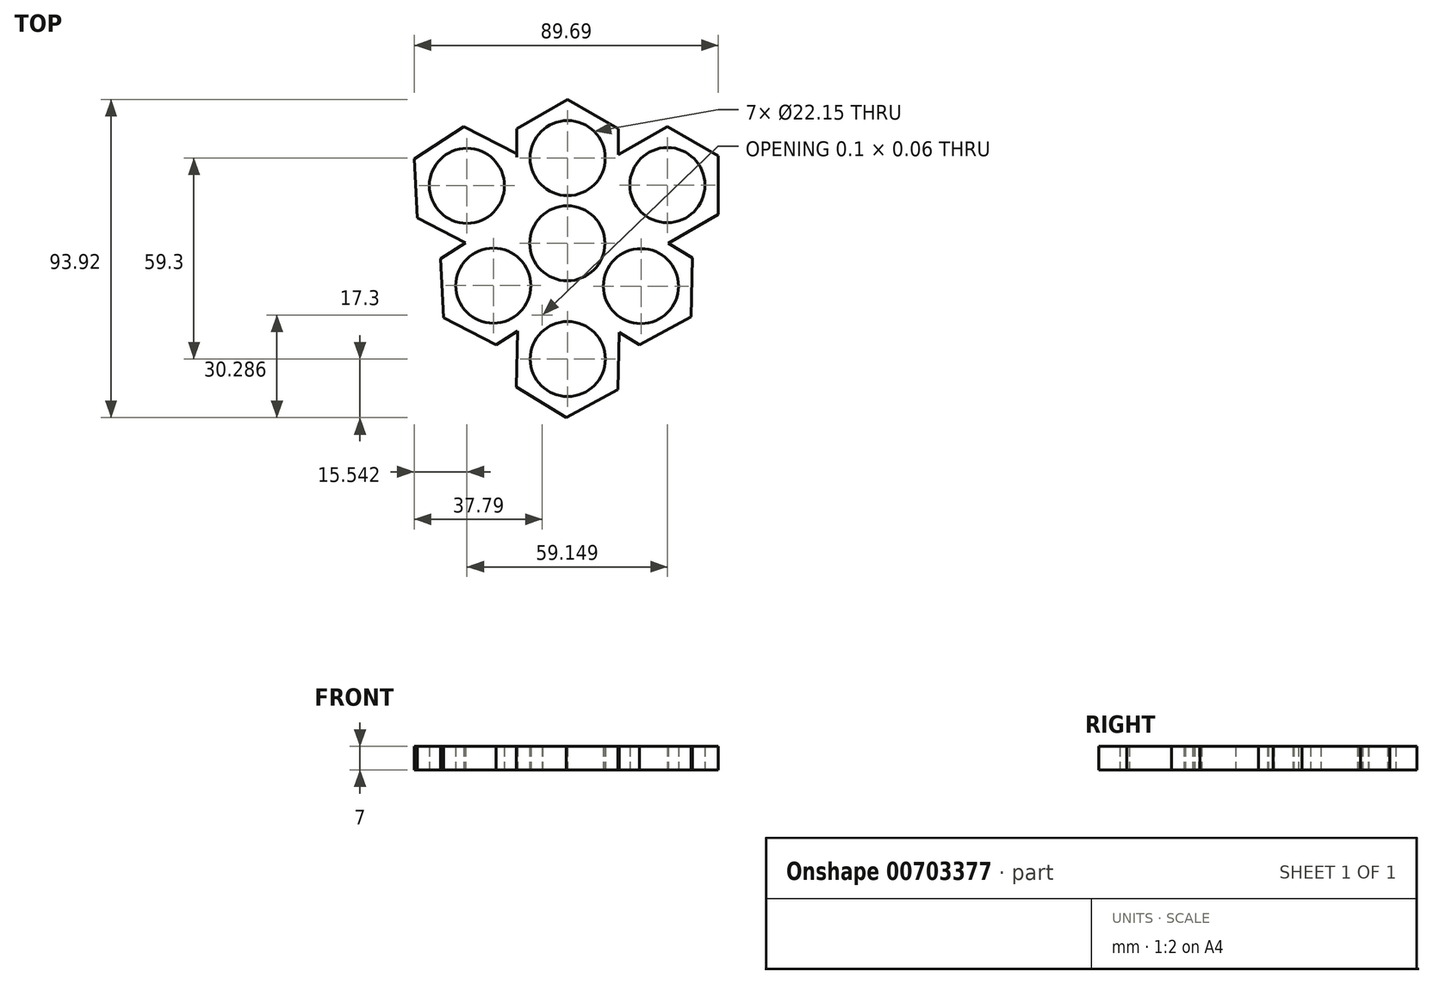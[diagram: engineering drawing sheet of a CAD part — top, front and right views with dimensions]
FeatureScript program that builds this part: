
annotation { "Feature Type Name" : "Feature", "Feature Type Description" : "" }
export const myFeature = defineFeature(function(context is Context, id is Id, definition is map)
    precondition{}
    {
        {
            var Q0;
            Q0=qCreatedBy(makeId("Top.planeOp"),FACE);
            var sketch = newSketch(context, id + "F0", { "sketchPlane" : qUnion([Q0])});
            skCircle(sketch, "E0.cCircle", {"center": v(0, 0) * mm, "radius": 12.57 * mm, "construction": true});
            skLineSegment(sketch, "E0.0", {"start": v(0.1, 25.15) * mm, "end": v(21.73, -12.66) * mm});
            skLineSegment(sketch, "E0.1", {"start": v(21.73, -12.66) * mm, "end": v(-21.83, -12.5) * mm});
            skLineSegment(sketch, "E0.2", {"start": v(-21.83, -12.5) * mm, "end": v(0.1, 25.15) * mm});
            skPoint(sketch, "E0.0.midPoint", {"position": v(10.91, 6.25) * mm});
            skCircle(sketch, "E1.cCircle", {"center": v(0.1, 25.15) * mm, "radius": 15 * mm, "construction": true});
            skLineSegment(sketch, "E1.0", {"start": v(15.1, 33.81) * mm, "end": v(15.1, 16.49) * mm});
            skLineSegment(sketch, "E1.1", {"start": v(15.1, 16.49) * mm, "end": v(0.1, 7.83) * mm});
            skLineSegment(sketch, "E1.2", {"start": v(0.1, 7.83) * mm, "end": v(-14.9, 16.49) * mm});
            skLineSegment(sketch, "E1.3", {"start": v(-14.9, 16.49) * mm, "end": v(-14.9, 33.81) * mm});
            skLineSegment(sketch, "E1.4", {"start": v(-14.9, 33.81) * mm, "end": v(0.1, 42.47) * mm});
            skLineSegment(sketch, "E1.5", {"start": v(0.1, 42.47) * mm, "end": v(15.1, 33.81) * mm});
            skPoint(sketch, "E1.0.midPoint", {"position": v(15.1, 25.15) * mm});
            skCircle(sketch, "E2.cCircle", {"center": v(21.73, -12.66) * mm, "radius": 14.99 * mm, "construction": true});
            skLineSegment(sketch, "E2.0", {"start": v(36.92, -4.34) * mm, "end": v(36.52, -21.65) * mm});
            skLineSegment(sketch, "E2.1", {"start": v(36.52, -21.65) * mm, "end": v(21.34, -29.96) * mm});
            skLineSegment(sketch, "E2.2", {"start": v(21.34, -29.96) * mm, "end": v(6.55, -20.97) * mm});
            skLineSegment(sketch, "E2.3", {"start": v(6.55, -20.97) * mm, "end": v(6.95, -3.66) * mm});
            skLineSegment(sketch, "E2.4", {"start": v(6.95, -3.66) * mm, "end": v(22.13, 4.65) * mm});
            skLineSegment(sketch, "E2.5", {"start": v(22.13, 4.65) * mm, "end": v(36.92, -4.34) * mm});
            skPoint(sketch, "E2.0.midPoint", {"position": v(36.72, -13) * mm});
            skCircle(sketch, "E3.cCircle", {"center": v(-21.83, -12.5) * mm, "radius": 15.12 * mm, "construction": true});
            skLineSegment(sketch, "E3.0", {"start": v(-20.96, -29.93) * mm, "end": v(-36.5, -21.97) * mm});
            skLineSegment(sketch, "E3.1", {"start": v(-36.5, -21.97) * mm, "end": v(-37.37, -4.53) * mm});
            skLineSegment(sketch, "E3.2", {"start": v(-37.37, -4.53) * mm, "end": v(-22.7, 4.95) * mm});
            skLineSegment(sketch, "E3.3", {"start": v(-22.7, 4.95) * mm, "end": v(-7.16, -3.02) * mm});
            skLineSegment(sketch, "E3.4", {"start": v(-7.16, -3.02) * mm, "end": v(-6.29, -20.46) * mm});
            skLineSegment(sketch, "E3.5", {"start": v(-6.29, -20.46) * mm, "end": v(-20.96, -29.93) * mm});
            skPoint(sketch, "E3.0.midPoint", {"position": v(-28.73, -25.95) * mm});
            skCircle(sketch, "E4", {"center": v(0.1, 25.15) * mm, "radius": 11.07 * mm});
            skCircle(sketch, "E5", {"center": v(0, 0) * mm, "radius": 11.07 * mm});
            skCircle(sketch, "E6", {"center": v(-21.83, -12.5) * mm, "radius": 11.07 * mm});
            skCircle(sketch, "E7", {"center": v(21.73, -12.66) * mm, "radius": 11.07 * mm});
            skCircle(sketch, "E8.cCircle", {"center": v(0, 0) * mm, "radius": 17.07 * mm, "construction": true});
            skLineSegment(sketch, "E8.0", {"start": v(29.52, 17.17) * mm, "end": v(0.1, -34.15) * mm});
            skLineSegment(sketch, "E8.1", {"start": v(0.1, -34.15) * mm, "end": v(-29.63, 16.98) * mm});
            skLineSegment(sketch, "E8.2", {"start": v(-29.63, 16.98) * mm, "end": v(29.52, 17.17) * mm});
            skPoint(sketch, "E8.0.midPoint", {"position": v(14.81, -8.5) * mm});
            skCircle(sketch, "E9.cCircle", {"center": v(29.52, 17.17) * mm, "radius": 15 * mm, "construction": true});
            skLineSegment(sketch, "E9.0", {"start": v(44.52, 8.5) * mm, "end": v(29.52, -0.15) * mm});
            skLineSegment(sketch, "E9.1", {"start": v(29.52, -0.15) * mm, "end": v(14.52, 8.5) * mm});
            skLineSegment(sketch, "E9.2", {"start": v(14.52, 8.5) * mm, "end": v(14.52, 25.83) * mm});
            skLineSegment(sketch, "E9.3", {"start": v(14.52, 25.83) * mm, "end": v(29.52, 34.49) * mm});
            skLineSegment(sketch, "E9.4", {"start": v(29.52, 34.49) * mm, "end": v(44.52, 25.83) * mm});
            skLineSegment(sketch, "E9.5", {"start": v(44.52, 25.83) * mm, "end": v(44.52, 8.5) * mm});
            skPoint(sketch, "E9.0.midPoint", {"position": v(37.02, 4.18) * mm});
            skCircle(sketch, "E10.cCircle", {"center": v(0.1, -34.15) * mm, "radius": 14.99 * mm, "construction": true});
            skLineSegment(sketch, "E10.0", {"start": v(14.9, -43.14) * mm, "end": v(-0.29, -51.45) * mm});
            skLineSegment(sketch, "E10.1", {"start": v(-0.29, -51.45) * mm, "end": v(-15.08, -42.46) * mm});
            skLineSegment(sketch, "E10.2", {"start": v(-15.08, -42.46) * mm, "end": v(-14.68, -25.16) * mm});
            skLineSegment(sketch, "E10.3", {"start": v(-14.68, -25.16) * mm, "end": v(0.5, -16.85) * mm});
            skLineSegment(sketch, "E10.4", {"start": v(0.5, -16.85) * mm, "end": v(15.29, -25.84) * mm});
            skLineSegment(sketch, "E10.5", {"start": v(15.29, -25.84) * mm, "end": v(14.9, -43.14) * mm});
            skPoint(sketch, "E10.0.midPoint", {"position": v(7.3, -47.3) * mm});
            skCircle(sketch, "E11.cCircle", {"center": v(-29.63, 16.98) * mm, "radius": 15.12 * mm, "construction": true});
            skLineSegment(sketch, "E11.0", {"start": v(-44.3, 7.5) * mm, "end": v(-45.17, 24.95) * mm});
            skLineSegment(sketch, "E11.1", {"start": v(-45.17, 24.95) * mm, "end": v(-30.5, 34.42) * mm});
            skLineSegment(sketch, "E11.2", {"start": v(-30.5, 34.42) * mm, "end": v(-14.96, 26.46) * mm});
            skLineSegment(sketch, "E11.3", {"start": v(-14.96, 26.46) * mm, "end": v(-14.09, 9.02) * mm});
            skLineSegment(sketch, "E11.4", {"start": v(-14.09, 9.02) * mm, "end": v(-28.76, -0.46) * mm});
            skLineSegment(sketch, "E11.5", {"start": v(-28.76, -0.46) * mm, "end": v(-44.3, 7.5) * mm});
            skPoint(sketch, "E11.0.midPoint", {"position": v(-44.73, 16.23) * mm});
            skCircle(sketch, "E12", {"center": v(29.52, 17.17) * mm, "radius": 11.07 * mm});
            skCircle(sketch, "E13", {"center": v(-29.63, 16.98) * mm, "radius": 11.07 * mm});
            skCircle(sketch, "E14", {"center": v(0.1, -34.15) * mm, "radius": 11.07 * mm});
            skSolve(sketch);
        }
        {
            var Q0;
            {var subQ5=sQuery(id+"F0.wireOp",EDGE,"E11.0");Q0=makeQuery(id+"F0.imprint","IMPRINT",FACE,{"disambiguationData":[TD([[makeQuery(id+"F0.imprint","IMPRINT",EDGE,{"derivedFrom":subQ5}),-1.0]])]});}
            var Q1;
            {var subQ5=sQuery(id+"F0.wireOp",EDGE,"E1.3");var subQ6=sQuery(id+"F0.wireOp",EDGE,"E1.2");var subQ7=makeQuery(id+"F0.imprint","INTERSECT",VERTEX,{"derivedFrom":[subQ6,subQ5]});Q1=makeQuery(id+"F0.imprint","IMPRINT",FACE,{"disambiguationData":[TD([[makeQuery(id+"F0.imprint","IMPRINT",EDGE,{"disambiguationData":[TD([[subQ7,1.0]])],"derivedFrom":subQ6}),1.0]])]});}
            var Q2;
            {var subQ5=sQuery(id+"F0.wireOp",EDGE,"E4");var subQ8=sQuery(id+"F0.wireOp",EDGE,"E0.0");var subQ11=makeQuery(id+"F0.imprint","INTERSECT",VERTEX,{"derivedFrom":[subQ8,subQ5]});Q2=makeQuery(id+"F0.imprint","IMPRINT",FACE,{"disambiguationData":[TD([[makeQuery(id+"F0.imprint","IMPRINT",EDGE,{"disambiguationData":[TD([[subQ11,-1.0]])],"derivedFrom":subQ8}),-1.0]])]});}
            var Q3;
            {var subQ0=sQuery(id+"F0.wireOp",EDGE,"E4");var subQ1=sQuery(id+"F0.wireOp",EDGE,"E0.0");var subQ2=makeQuery(id+"F0.imprint","INTERSECT",VERTEX,{"derivedFrom":[subQ1,subQ0]});Q3=makeQuery(id+"F0.imprint","IMPRINT",FACE,{"disambiguationData":[TD([[makeQuery(id+"F0.imprint","IMPRINT",EDGE,{"disambiguationData":[TD([[subQ2,-1.0]])],"derivedFrom":subQ1}),1.0]])]});}
            var Q4;
            {var subQ5=sQuery(id+"F0.wireOp",EDGE,"E1.2");var subQ6=sQuery(id+"F0.wireOp",EDGE,"E0.2");var subQ7=makeQuery(id+"F0.imprint","INTERSECT",VERTEX,{"derivedFrom":[subQ6,subQ5]});Q4=makeQuery(id+"F0.imprint","IMPRINT",FACE,{"disambiguationData":[TD([[makeQuery(id+"F0.imprint","IMPRINT",EDGE,{"disambiguationData":[TD([[subQ7,-1.0]])],"derivedFrom":subQ6}),1.0]])]});}
            var Q5;
            {var subQ11=sQuery(id+"F0.wireOp",EDGE,"E2.0");Q5=makeQuery(id+"F0.imprint","IMPRINT",FACE,{"disambiguationData":[TD([[makeQuery(id+"F0.imprint","IMPRINT",EDGE,{"derivedFrom":subQ11}),-1.0]])]});}
            var Q6;
            {var subQ0=sQuery(id+"F0.wireOp",EDGE,"E2.4");var subQ1=sQuery(id+"F0.wireOp",EDGE,"E0.0");var subQ2=makeQuery(id+"F0.imprint","INTERSECT",VERTEX,{"derivedFrom":[subQ1,subQ0]});Q6=makeQuery(id+"F0.imprint","IMPRINT",FACE,{"disambiguationData":[TD([[makeQuery(id+"F0.imprint","IMPRINT",EDGE,{"disambiguationData":[TD([[subQ2,-1.0]])],"derivedFrom":subQ1}),-1.0]])]});}
            var Q7;
            {var subQ1=sQuery(id+"F0.wireOp",EDGE,"E0.0");var subQ5=sQuery(id+"F0.wireOp",EDGE,"E2.4");var subQ6=makeQuery(id+"F0.imprint","INTERSECT",VERTEX,{"derivedFrom":[subQ1,subQ5]});Q7=makeQuery(id+"F0.imprint","IMPRINT",FACE,{"disambiguationData":[TD([[makeQuery(id+"F0.imprint","IMPRINT",EDGE,{"disambiguationData":[TD([[subQ6,-1.0]])],"derivedFrom":subQ1}),1.0]])]});}
            var Q8;
            {var subQ6=sQuery(id+"F0.wireOp",EDGE,"E2.2");var subQ9=sQuery(id+"F0.wireOp",EDGE,"E2.3");var subQ10=makeQuery(id+"F0.imprint","INTERSECT",VERTEX,{"derivedFrom":[subQ6,subQ9]});Q8=makeQuery(id+"F0.imprint","IMPRINT",FACE,{"disambiguationData":[TD([[makeQuery(id+"F0.imprint","IMPRINT",EDGE,{"disambiguationData":[TD([[subQ10,1.0]])],"derivedFrom":subQ6}),1.0]])]});}
            var Q9;
            {var subQ1=sQuery(id+"F0.wireOp",EDGE,"E0.1");var subQ6=sQuery(id+"F0.wireOp",EDGE,"E3.4");var subQ8=makeQuery(id+"F0.imprint","INTERSECT",VERTEX,{"derivedFrom":[subQ1,subQ6]});Q9=makeQuery(id+"F0.imprint","IMPRINT",FACE,{"disambiguationData":[TD([[makeQuery(id+"F0.imprint","IMPRINT",EDGE,{"disambiguationData":[TD([[subQ8,-1.0]])],"derivedFrom":subQ1}),1.0]])]});}
            var Q10;
            {var subQ10=sQuery(id+"F0.wireOp",EDGE,"E3.0");Q10=makeQuery(id+"F0.imprint","IMPRINT",FACE,{"disambiguationData":[TD([[makeQuery(id+"F0.imprint","IMPRINT",EDGE,{"derivedFrom":subQ10}),-1.0]])]});}
            var Q11;
            {var subQ0=sQuery(id+"F0.wireOp",EDGE,"E3.4");var subQ1=sQuery(id+"F0.wireOp",EDGE,"E0.1");var subQ2=makeQuery(id+"F0.imprint","INTERSECT",VERTEX,{"derivedFrom":[subQ1,subQ0]});Q11=makeQuery(id+"F0.imprint","IMPRINT",FACE,{"disambiguationData":[TD([[makeQuery(id+"F0.imprint","IMPRINT",EDGE,{"disambiguationData":[TD([[subQ2,-1.0]])],"derivedFrom":subQ1}),-1.0]])]});}
            var Q12;
            {var subQ0=sQuery(id+"F0.wireOp",EDGE,"E6");var subQ1=sQuery(id+"F0.wireOp",EDGE,"E0.2");var subQ2=makeQuery(id+"F0.imprint","INTERSECT",VERTEX,{"derivedFrom":[subQ1,subQ0]});Q12=makeQuery(id+"F0.imprint","IMPRINT",FACE,{"disambiguationData":[TD([[makeQuery(id+"F0.imprint","IMPRINT",EDGE,{"disambiguationData":[TD([[subQ2,-1.0]])],"derivedFrom":subQ1}),1.0]])]});}
            var Q13;
            {var subQ1=sQuery(id+"F0.wireOp",EDGE,"E3.3");var subQ5=sQuery(id+"F0.wireOp",EDGE,"E3.2");var subQ6=makeQuery(id+"F0.imprint","INTERSECT",VERTEX,{"derivedFrom":[subQ5,subQ1]});Q13=makeQuery(id+"F0.imprint","IMPRINT",FACE,{"disambiguationData":[TD([[makeQuery(id+"F0.imprint","IMPRINT",EDGE,{"disambiguationData":[TD([[subQ6,1.0]])],"derivedFrom":subQ5}),-1.0]])]});}
            var Q14;
            {var subQ3=sQuery(id+"F0.wireOp",EDGE,"E0.1");var subQ5=sQuery(id+"F0.wireOp",EDGE,"E2.3");var subQ6=makeQuery(id+"F0.imprint","INTERSECT",VERTEX,{"derivedFrom":[subQ3,subQ5]});Q14=makeQuery(id+"F0.imprint","IMPRINT",FACE,{"disambiguationData":[TD([[makeQuery(id+"F0.imprint","IMPRINT",EDGE,{"disambiguationData":[TD([[subQ6,-1.0]])],"derivedFrom":subQ3}),1.0]])]});}
            var Q15;
            {var subQ0=sQuery(id+"F0.wireOp",EDGE,"E2.3");var subQ1=sQuery(id+"F0.wireOp",EDGE,"E0.1");var subQ2=makeQuery(id+"F0.imprint","INTERSECT",VERTEX,{"derivedFrom":[subQ1,subQ0]});Q15=makeQuery(id+"F0.imprint","IMPRINT",FACE,{"disambiguationData":[TD([[makeQuery(id+"F0.imprint","IMPRINT",EDGE,{"disambiguationData":[TD([[subQ2,-1.0]])],"derivedFrom":subQ1}),-1.0]])]});}
            var Q16;
            {var subQ0=sQuery(id+"F0.wireOp",EDGE,"E1.1");var subQ1=sQuery(id+"F0.wireOp",EDGE,"E0.0");var subQ2=makeQuery(id+"F0.imprint","INTERSECT",VERTEX,{"derivedFrom":[subQ1,subQ0]});Q16=makeQuery(id+"F0.imprint","IMPRINT",FACE,{"disambiguationData":[TD([[makeQuery(id+"F0.imprint","IMPRINT",EDGE,{"disambiguationData":[TD([[subQ2,-1.0]])],"derivedFrom":subQ1}),-1.0]])]});}
            var Q17;
            {var subQ0=sQuery(id+"F0.wireOp",EDGE,"E1.1");var subQ1=sQuery(id+"F0.wireOp",EDGE,"E0.0");var subQ2=makeQuery(id+"F0.imprint","INTERSECT",VERTEX,{"derivedFrom":[subQ1,subQ0]});Q17=makeQuery(id+"F0.imprint","IMPRINT",FACE,{"disambiguationData":[TD([[makeQuery(id+"F0.imprint","IMPRINT",EDGE,{"disambiguationData":[TD([[subQ2,-1.0]])],"derivedFrom":subQ1}),1.0]])]});}
            var Q18;
            {var subQ0=sQuery(id+"F0.wireOp",EDGE,"E1.4");Q18=makeQuery(id+"F0.imprint","IMPRINT",FACE,{"disambiguationData":[TD([[makeQuery(id+"F0.imprint","IMPRINT",EDGE,{"derivedFrom":subQ0}),-1.0]])]});}
            var Q19;
            {var subQ10=sQuery(id+"F0.wireOp",EDGE,"E9.4");Q19=makeQuery(id+"F0.imprint","IMPRINT",FACE,{"disambiguationData":[TD([[makeQuery(id+"F0.imprint","IMPRINT",EDGE,{"derivedFrom":subQ10}),-1.0]])]});}
            var Q20;
            {var subQ5=sQuery(id+"F0.wireOp",EDGE,"E3.3");var subQ6=sQuery(id+"F0.wireOp",EDGE,"E0.2");var subQ7=makeQuery(id+"F0.imprint","INTERSECT",VERTEX,{"derivedFrom":[subQ6,subQ5]});Q20=makeQuery(id+"F0.imprint","IMPRINT",FACE,{"disambiguationData":[TD([[makeQuery(id+"F0.imprint","IMPRINT",EDGE,{"disambiguationData":[TD([[subQ7,-1.0]])],"derivedFrom":subQ6}),1.0]])]});}
            var Q21;
            {var subQ0=sQuery(id+"F0.wireOp",EDGE,"E3.3");var subQ1=sQuery(id+"F0.wireOp",EDGE,"E0.2");var subQ2=makeQuery(id+"F0.imprint","INTERSECT",VERTEX,{"derivedFrom":[subQ1,subQ0]});Q21=makeQuery(id+"F0.imprint","IMPRINT",FACE,{"disambiguationData":[TD([[makeQuery(id+"F0.imprint","IMPRINT",EDGE,{"disambiguationData":[TD([[subQ2,-1.0]])],"derivedFrom":subQ1}),-1.0]])]});}
            var Q22;
            {var subQ0=sQuery(id+"F0.wireOp",EDGE,"E8.1");var subQ1=sQuery(id+"F0.wireOp",EDGE,"E3.3");var subQ2=makeQuery(id+"F0.imprint","INTERSECT",VERTEX,{"derivedFrom":[subQ1,subQ0]});Q22=makeQuery(id+"F0.imprint","IMPRINT",FACE,{"disambiguationData":[TD([[makeQuery(id+"F0.imprint","IMPRINT",EDGE,{"disambiguationData":[TD([[subQ2,-1.0]])],"derivedFrom":subQ1}),-1.0]])]});}
            var Q23;
            {var subQ0=sQuery(id+"F0.wireOp",EDGE,"E1.3");var subQ1=sQuery(id+"F0.wireOp",EDGE,"E1.2");var subQ2=makeQuery(id+"F0.imprint","INTERSECT",VERTEX,{"derivedFrom":[subQ1,subQ0]});Q23=makeQuery(id+"F0.imprint","IMPRINT",FACE,{"disambiguationData":[TD([[makeQuery(id+"F0.imprint","IMPRINT",EDGE,{"disambiguationData":[TD([[subQ2,1.0]])],"derivedFrom":subQ1}),-1.0]])]});}
            var Q24;
            {var subQ0=sQuery(id+"F0.wireOp",EDGE,"E11.3");var subQ1=sQuery(id+"F0.wireOp",EDGE,"E1.3");var subQ2=makeQuery(id+"F0.imprint","INTERSECT",VERTEX,{"derivedFrom":[subQ1,subQ0]});Q24=makeQuery(id+"F0.imprint","IMPRINT",FACE,{"disambiguationData":[TD([[makeQuery(id+"F0.imprint","IMPRINT",EDGE,{"disambiguationData":[TD([[subQ2,1.0]])],"derivedFrom":subQ1}),-1.0]])]});}
            var Q25;
            {var subQ0=sQuery(id+"F0.wireOp",EDGE,"E9.3");var subQ1=sQuery(id+"F0.wireOp",EDGE,"E1.0");var subQ2=makeQuery(id+"F0.imprint","INTERSECT",VERTEX,{"derivedFrom":[subQ1,subQ0]});Q25=makeQuery(id+"F0.imprint","IMPRINT",FACE,{"disambiguationData":[TD([[makeQuery(id+"F0.imprint","IMPRINT",EDGE,{"disambiguationData":[TD([[subQ2,-1.0]])],"derivedFrom":subQ1}),-1.0]])]});}
            var Q26;
            {var subQ0=sQuery(id+"F0.wireOp",EDGE,"E1.1");var subQ1=sQuery(id+"F0.wireOp",EDGE,"E1.0");var subQ2=makeQuery(id+"F0.imprint","INTERSECT",VERTEX,{"derivedFrom":[subQ1,subQ0]});Q26=makeQuery(id+"F0.imprint","IMPRINT",FACE,{"disambiguationData":[TD([[makeQuery(id+"F0.imprint","IMPRINT",EDGE,{"disambiguationData":[TD([[subQ2,1.0]])],"derivedFrom":subQ1}),-1.0]])]});}
            var Q27;
            {var subQ9=sQuery(id+"F0.wireOp",EDGE,"E1.1");var subQ10=sQuery(id+"F0.wireOp",EDGE,"E1.0");var subQ11=makeQuery(id+"F0.imprint","INTERSECT",VERTEX,{"derivedFrom":[subQ10,subQ9]});Q27=makeQuery(id+"F0.imprint","IMPRINT",FACE,{"disambiguationData":[TD([[makeQuery(id+"F0.imprint","IMPRINT",EDGE,{"disambiguationData":[TD([[subQ11,1.0]])],"derivedFrom":subQ10}),1.0]])]});}
            var Q28;
            {var subQ0=sQuery(id+"F0.wireOp",EDGE,"E9.0");var subQ1=sQuery(id+"F0.wireOp",EDGE,"E2.5");var subQ2=makeQuery(id+"F0.imprint","INTERSECT",VERTEX,{"derivedFrom":[subQ1,subQ0]});Q28=makeQuery(id+"F0.imprint","IMPRINT",FACE,{"disambiguationData":[TD([[makeQuery(id+"F0.imprint","IMPRINT",EDGE,{"disambiguationData":[TD([[subQ2,1.0]])],"derivedFrom":subQ1}),-1.0]])]});}
            var Q29;
            {var subQ0=sQuery(id+"F0.wireOp",EDGE,"E2.5");var subQ1=sQuery(id+"F0.wireOp",EDGE,"E2.4");var subQ2=makeQuery(id+"F0.imprint","INTERSECT",VERTEX,{"derivedFrom":[subQ1,subQ0]});Q29=makeQuery(id+"F0.imprint","IMPRINT",FACE,{"disambiguationData":[TD([[makeQuery(id+"F0.imprint","IMPRINT",EDGE,{"disambiguationData":[TD([[subQ2,1.0]])],"derivedFrom":subQ1}),-1.0]])]});}
            var Q30;
            {var subQ0=sQuery(id+"F0.wireOp",EDGE,"E10.2");var subQ1=sQuery(id+"F0.wireOp",EDGE,"E3.5");var subQ2=makeQuery(id+"F0.imprint","INTERSECT",VERTEX,{"derivedFrom":[subQ1,subQ0]});Q30=makeQuery(id+"F0.imprint","IMPRINT",FACE,{"disambiguationData":[TD([[makeQuery(id+"F0.imprint","IMPRINT",EDGE,{"disambiguationData":[TD([[subQ2,1.0]])],"derivedFrom":subQ1}),-1.0]])]});}
            var Q31;
            {var subQ5=sQuery(id+"F0.wireOp",EDGE,"E10.0");Q31=makeQuery(id+"F0.imprint","IMPRINT",FACE,{"disambiguationData":[TD([[makeQuery(id+"F0.imprint","IMPRINT",EDGE,{"derivedFrom":subQ5}),-1.0]])]});}
            var Q32;
            {var subQ0=sQuery(id+"F0.wireOp",EDGE,"E10.5");var subQ1=sQuery(id+"F0.wireOp",EDGE,"E2.2");var subQ2=makeQuery(id+"F0.imprint","INTERSECT",VERTEX,{"derivedFrom":[subQ1,subQ0]});Q32=makeQuery(id+"F0.imprint","IMPRINT",FACE,{"disambiguationData":[TD([[makeQuery(id+"F0.imprint","IMPRINT",EDGE,{"disambiguationData":[TD([[subQ2,-1.0]])],"derivedFrom":subQ1}),-1.0]])]});}
            var Q33;
            {var subQ0=sQuery(id+"F0.wireOp",EDGE,"E2.3");var subQ1=sQuery(id+"F0.wireOp",EDGE,"E2.2");var subQ2=makeQuery(id+"F0.imprint","INTERSECT",VERTEX,{"derivedFrom":[subQ1,subQ0]});Q33=makeQuery(id+"F0.imprint","IMPRINT",FACE,{"disambiguationData":[TD([[makeQuery(id+"F0.imprint","IMPRINT",EDGE,{"disambiguationData":[TD([[subQ2,1.0]])],"derivedFrom":subQ1}),-1.0]])]});}
            var Q34;
            {var subQ1=sQuery(id+"F0.wireOp",EDGE,"E7");var subQ6=sQuery(id+"F0.wireOp",EDGE,"E0.1");var subQ9=makeQuery(id+"F0.imprint","INTERSECT",VERTEX,{"derivedFrom":[subQ6,subQ1]});Q34=makeQuery(id+"F0.imprint","IMPRINT",FACE,{"disambiguationData":[TD([[makeQuery(id+"F0.imprint","IMPRINT",EDGE,{"disambiguationData":[TD([[subQ9,-1.0]])],"derivedFrom":subQ6}),1.0]])]});}
            extrude(context, id + "F1", {"entities" : qUnion([Q0, Q1, Q2, Q3, Q4, Q5, Q6, Q7, Q8, Q9, Q10, Q11, Q12, Q13, Q14, Q15, Q16, Q17, Q18, Q19, Q20, Q21, Q22, Q23, Q24, Q25, Q26, Q27, Q28, Q29, Q30, Q31, Q32, Q33, Q34]), "depth" : 7 * mm, "offsetDistance" : 25 * mm});
        }
    });
